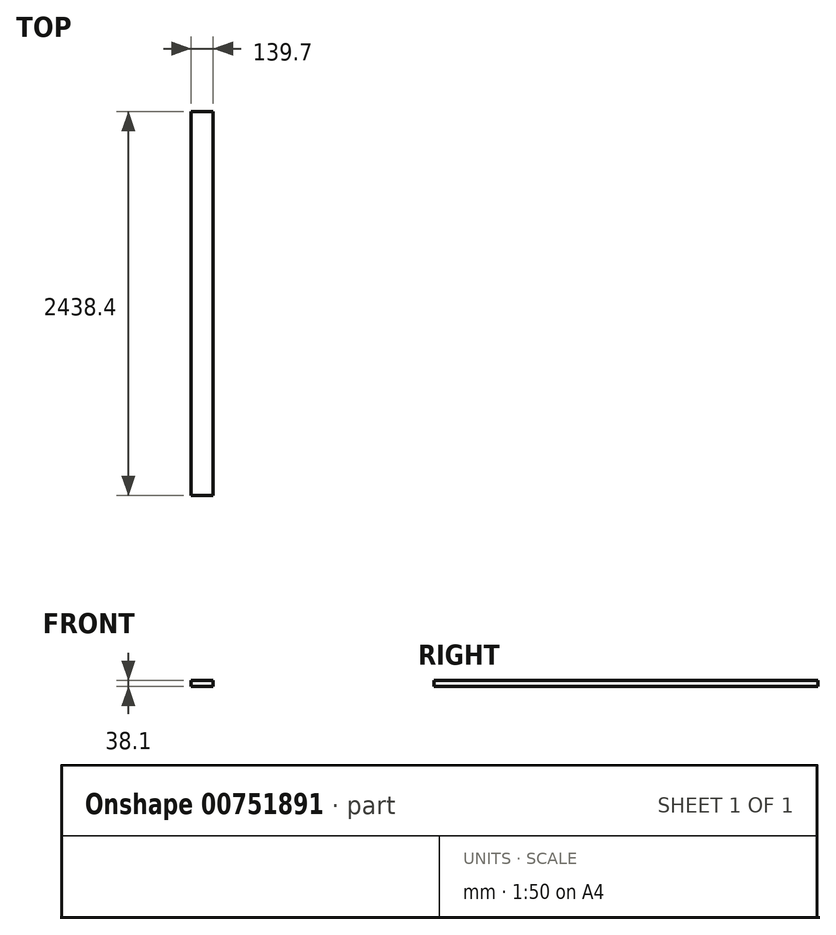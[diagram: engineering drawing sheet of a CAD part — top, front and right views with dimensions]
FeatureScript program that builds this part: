
annotation { "Feature Type Name" : "Feature", "Feature Type Description" : "" }
export const myFeature = defineFeature(function(context is Context, id is Id, definition is map)
    precondition{}
    {
        {
            var Q0;
            Q0=qCreatedBy(makeId("Front.planeOp"),FACE);
            var sketch = newSketch(context, id + "F0", { "sketchPlane" : qUnion([Q0])});
            skLineSegment(sketch, "E0.bottom", {"start": v(69.85, 19.05) * mm, "end": v(-69.85, 19.05) * mm});
            skLineSegment(sketch, "E0.top", {"start": v(69.85, -19.05) * mm, "end": v(-69.85, -19.05) * mm});
            skLineSegment(sketch, "E0.left", {"start": v(69.85, 19.05) * mm, "end": v(69.85, -19.05) * mm});
            skLineSegment(sketch, "E0.right", {"start": v(-69.85, 19.05) * mm, "end": v(-69.85, -19.05) * mm});
            skPoint(sketch, "E0.middle", {"position": v(0, 0) * mm});
            skSolve(sketch);
        }
        {
            var Q0;
            Q0=makeQuery(id+"F0.imprint","IMPRINT",FACE,{"disambiguationData":[TD([[makeQuery(id+"F0.imprint","IMPRINT",EDGE,{"derivedFrom":sQuery(id+"F0.wireOp",EDGE,"E0.bottom")}),1.0]])]});
            extrude(context, id + "F1", {"entities" : qUnion([Q0]), "depth" : 8 * 304.8 * mm, "offsetDistance" : 25.4 * mm});
        }
    });
